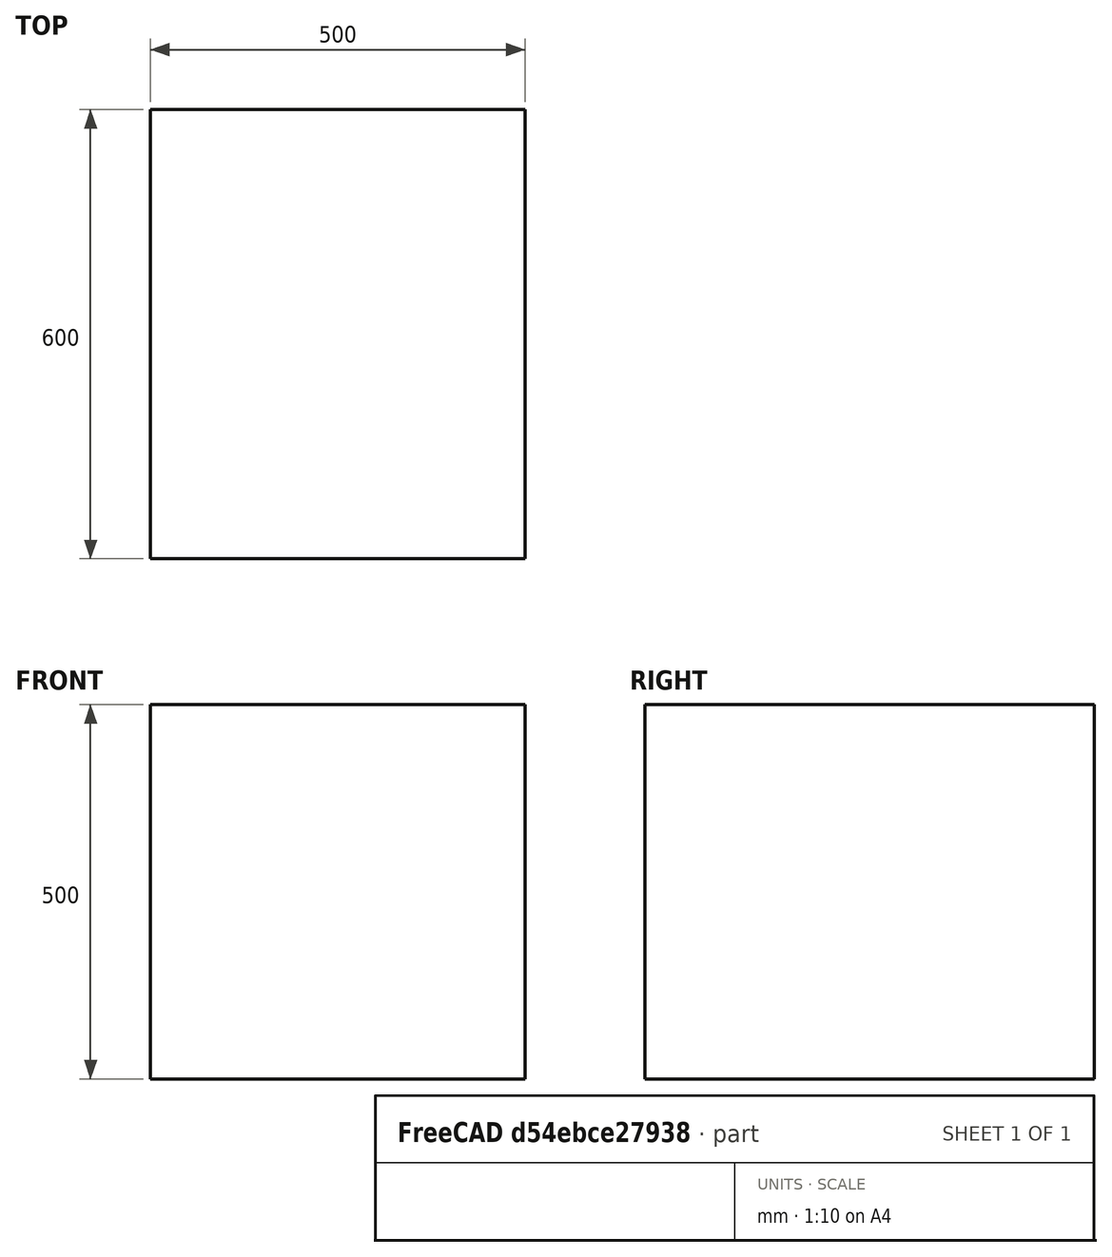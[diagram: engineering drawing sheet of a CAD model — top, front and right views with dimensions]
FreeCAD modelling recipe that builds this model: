
FCSTD DOCUMENT  (FreeCAD 0.19R24291 (Git))
Label: retangular
License: All rights reserved
LicenseURL: http://en.wikipedia.org/wiki/All_rights_reserved
objects: Sketcher::SketchObject×2, PartDesign::Pad×1, PartDesign::Body×1
note: 5 computed .brp shape members not serialized (recipe doc carries the construction recipe); baked Part::Feature solids carry a one-line shape summary decoded from their .brp

FEATURE [Sketcher::SketchObject] Sketch
  FullyConstrained = true
  MapMode = 5
  Support = -> [XY_Plane]
  sketch-geometry (4):
    g0: LineSegment StartX=0 StartY=600 StartZ=0 EndX=0 EndY=0 EndZ=0
    g1: LineSegment StartX=0 StartY=600 StartZ=0 EndX=500 EndY=600 EndZ=0
    g2: LineSegment StartX=500 StartY=600 StartZ=0 EndX=500 EndY=0 EndZ=0
    g3: LineSegment StartX=500 StartY=0 StartZ=0 EndX=0 EndY=0 EndZ=0
  constraints (11):
    c: Vertical(g0)
    c: Horizontal(g1)
    c: DistanceY(g0,g0) = 600
    c: Coincident(g0,g-1)
    c: DistanceX(g1,g1) = 500
    c: Coincident(g1,g0)
    c: Vertical(g2)
    c: Coincident(g2,g3)
    c: Horizontal(g3)
    c: Coincident(g2,g1)
    c: Coincident(g3,g0)
FEATURE [PartDesign::Pad] Pad
  Direction = (1,1,1)
  Length = 500
  Length2 = 100
  Profile = -> Sketch
  Type = 0
FEATURE [Sketcher::SketchObject] Sketch001
  FullyConstrained = true
  MapMode = 5
  Placement = pos=(0,0,0) rot=(1,0,0;1.5708rad)
  Support = -> [Pad]
FEATURE [PartDesign::Body] Body
  Group = -> [Sketch,Pad,Sketch001]
  Origin = -> Origin
  Tip = -> Pad
